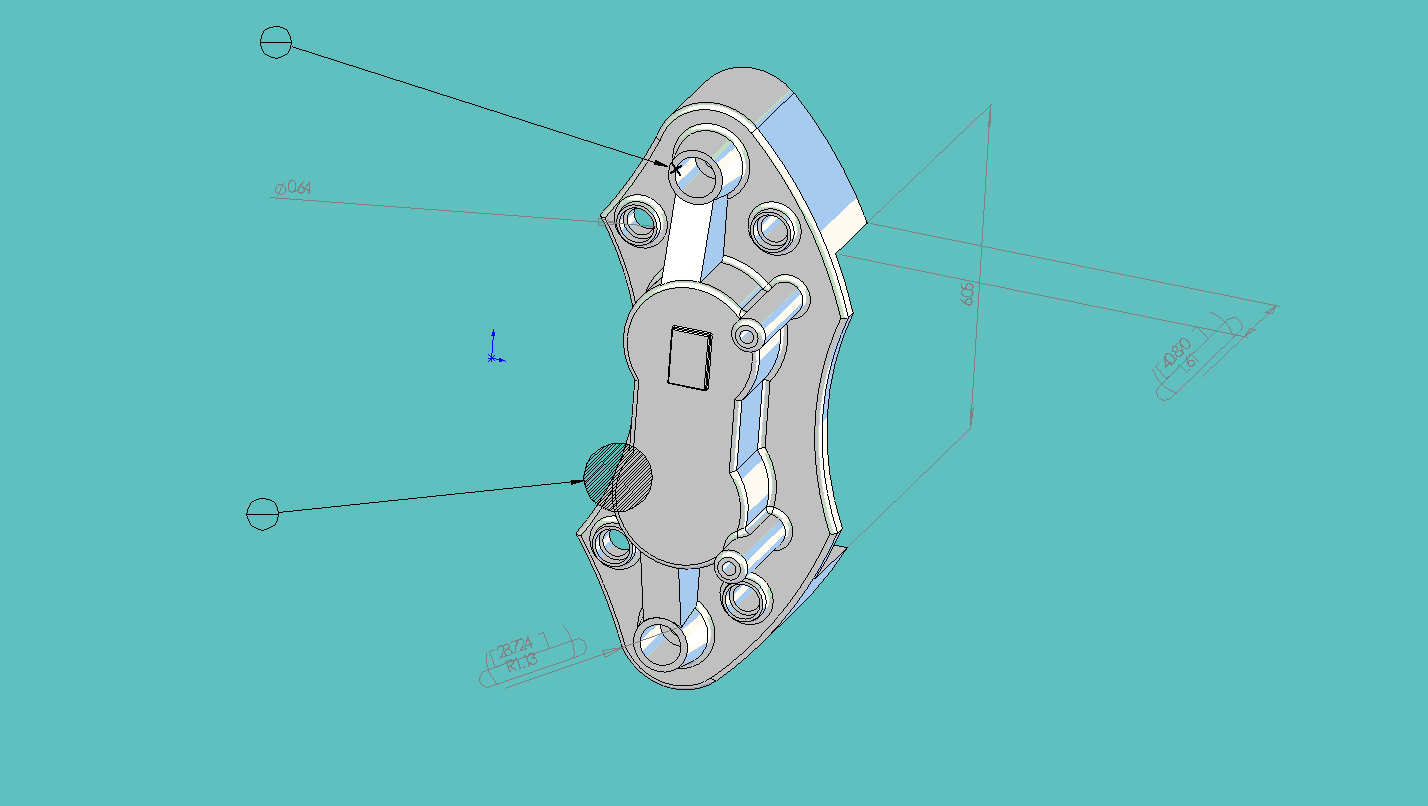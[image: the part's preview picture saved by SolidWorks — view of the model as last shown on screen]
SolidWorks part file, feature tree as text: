
SOLIDWORKS PART (.sldprt)
format: sldprt  version: not decoded by parser v0  size: 1,079,296 bytes
history: native  units: mm
features: sketch x25, cut_extrude x14, fillet x9, extrude x7, mirror x4, plane x3, material x1, chamfer x1, delete_body x1 + 1 further entry (+13 scaffold rows collapsed)
feature tree (79):
  scaffold x13  (default folders/planes/origin — collapsed)
  material  "Material <not specified>"
  "Detail Folder1"  RD2=16.253517mm
  sketch  "Sketch1"  dims[D1=63.5mm]
  extrude  "Extrude1"  Depth=31.75mm
  sketch  "Sketch5"  dims[D1=~43.962388mm]
  extrude  "Extrude2"  Depth=50.8mm
  sketch  "Sketch3"  dims[D1=50.0mm]
  cut_extrude  "Cut-Extrude1"  Depth=25.4mm
  sketch  "Sketch7"  dims[c1.D1=12.7mm c1.D2=12.7mm c2.D1=~13.906952mm c2.D2=25.0mm c2.D3=25.0mm c3.D1=~12.799272mm c3.D3=152.4mm]
  fillet  "Fillet1"  Radius=2.54mm
  fillet  "Fillet2"  Radius=2.54mm
  fillet  "Fillet3"  Radius=2.54mm
  sketch  "Sketch10"
  cut_extrude  "Cut-Extrude3"  [1 undecoded]
  plane  "Plane1"  Offset=10.16mm
  plane  "Plane2"  Offset=8.636mm
  sketch  "Sketch13"  dims[D1=273.05mm D2=137.16mm]
  cut_extrude  "Cut-Extrude4"  [1 undecoded]
  sketch  "Sketch14"
  cut_extrude  "Cut-Extrude5"  [1 undecoded]
  sketch  "Sketch15"
  extrude  "Extrude3"  Depth=53.18mm
  fillet  "Fillet4"  Radius=2.54mm
  sketch  "Sketch16"  dims[D1=~1.636236mm]
  cut_extrude  "Cut-Extrude6"  Depth=27.94mm
  fillet  "Fillet5"  Radius=2.54mm
  sketch  "Sketch17"
  extrude  "Extrude4"  Depth=2.54mm
  fillet  "Fillet6"  Radius=0.508mm
  chamfer  "Chamfer1"  Distance=1.27mm Angle=45deg
  sketch  "Sketch20"  dims[c1.D1=31.75mm c1.D2=25.4mm c2.D1=~20.003376mm]
  extrude  "Extrude5"  Depth=20.32mm
  cut_extrude  "Cut-Extrude8"  [1 undecoded]
  sketch  "Sketch21"  dims[D1=~4.108238mm]
  cut_extrude  "Cut-Extrude10"  Depth=25.4mm
  fillet  "Fillet7"  Radius=2.54mm
  sketch  "Sketch22"  dims[D1=10.16mm]
  cut_extrude  "Cut-Extrude11"  [1 undecoded]
  sketch  "Sketch24"
  cut_extrude  "Cut-Extrude12"  Depth=22.86mm
  sketch  "Sketch25"  dims[D1=20.574mm]
  extrude  "Extrude6"  Depth=5.08mm
  fillet  "Fillet8"  Radius=2.54mm
  sketch  "Sketch27"  dims[D1=~16.253517mm]
  cut_extrude  "Cut-Extrude15"  Depth=5.08mm
  mirror  "Mirror1"
  sketch  "Sketch29"  dims[D1=7.62mm]
  extrude  "Extrude7"  [1 undecoded]
  sketch  "Sketch30"
  sketch  "Sketch31"  dims[D1=5.08mm]
  cut_extrude  "Cut-Extrude18"  Depth=16.392582mm
  sketch  "Sketch32"  dims[D1=8.89mm]
  cut_extrude  "Cut-Extrude19"  Depth=16.392582mm
  cut_extrude  "Cut-Extrude20"  Depth=43.688mm
  sketch  "Sketch33"
  cut_extrude  "Cut-Extrude21"  Depth=59.69mm
  fillet  "Fillet11"  Radius=2.54mm
  plane  "Plane3"  Offset=94.488mm
  sketch  "Sketch34"  dims[D1=17.62mm]
  sketch  "Sketch36"
  mirror  "Rib3"
  sketch  "Sketch38"
  mirror  "Rib4"
  sketch  "Sketch40"
  mirror  "Rib5"
  delete_body  "Body-Delete1"
decode coverage: 40 of 61 modeling features carry decoded parameters; 1 rows unclassified (native names shown)
note: ~ marks probable driven/reference dimensions
note: 6 parameter values undecoded
summary: no parameter record found for 6 features
note: suppression state not decoded; provenance and decode notes live in map.json
